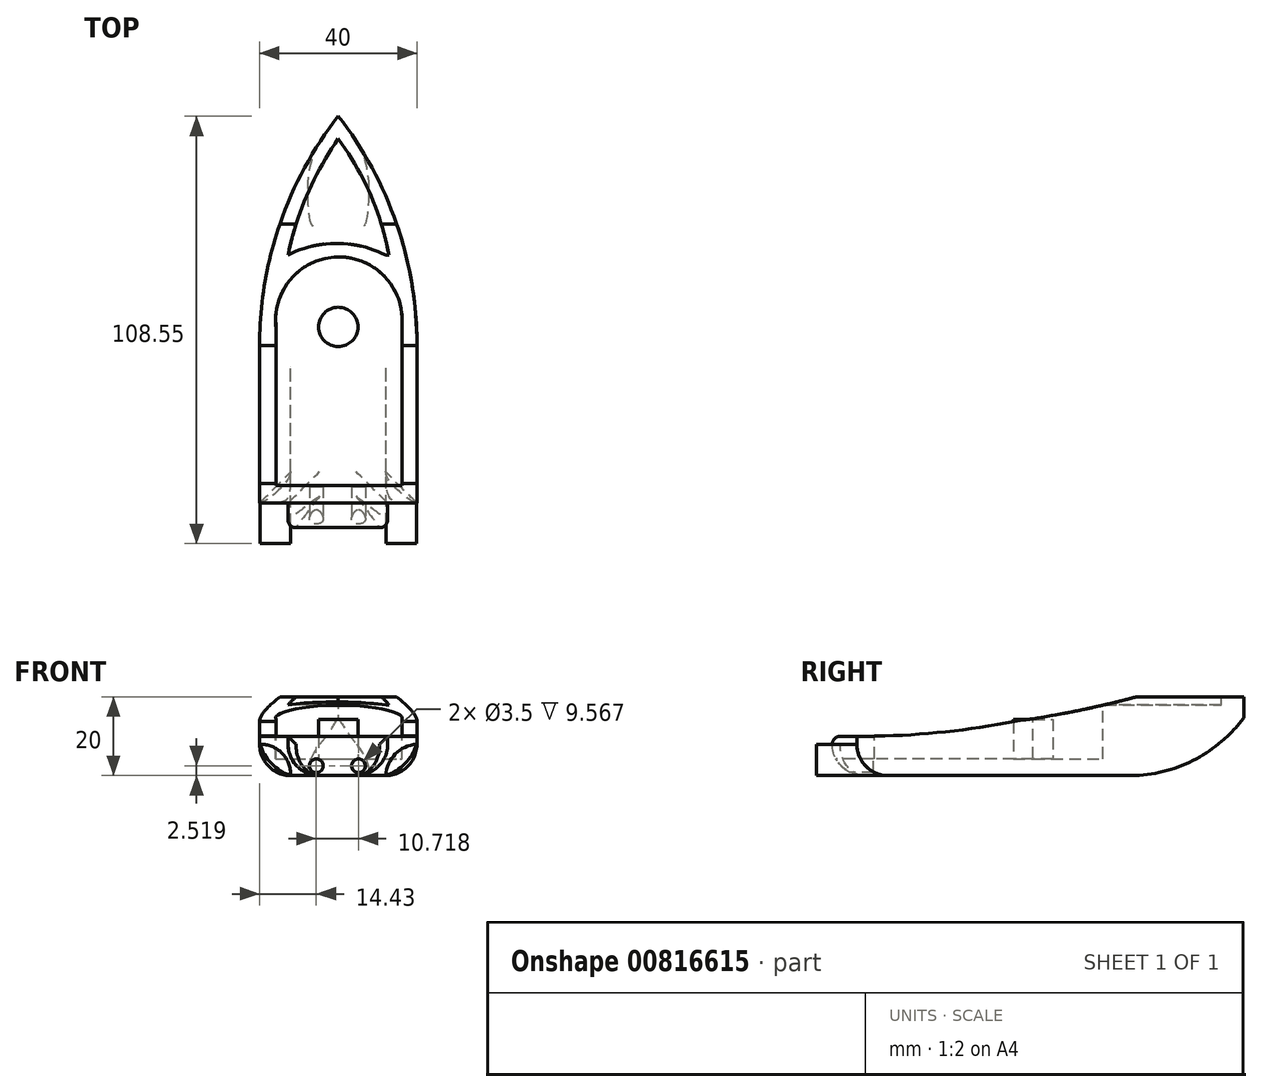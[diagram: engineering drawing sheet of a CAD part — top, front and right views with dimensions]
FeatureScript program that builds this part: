
annotation { "Feature Type Name" : "Feature", "Feature Type Description" : "" }
export const myFeature = defineFeature(function(context is Context, id is Id, definition is map)
    precondition{}
    {
        {
            var Q0;
            Q0=qCreatedBy(makeId("Top.planeOp"),FACE);
            var sketch = newSketch(context, id + "F0", { "sketchPlane" : qUnion([Q0])});
            skLineSegment(sketch, "E0.bottom", {"start": v(-20, 5.24) * mm, "end": v(20, 5.24) * mm});
            skLineSegment(sketch, "E0.top", {"start": v(-20, -34.76) * mm, "end": v(20, -34.76) * mm});
            skLineSegment(sketch, "E0.left", {"start": v(-20, 5.24) * mm, "end": v(-20, -34.76) * mm});
            skLineSegment(sketch, "E0.right", {"start": v(20, 5.24) * mm, "end": v(20, -34.76) * mm});
            skArc(sketch, "E1", {"start": v(0, 63.55) * mm, "mid": v(-14.86, 36.06) * mm, "end": v(-20, 5.24) * mm});
            skArc(sketch, "E2", {"start": v(20, 5.24) * mm, "mid": v(14.86, 36.06) * mm, "end": v(0, 63.55) * mm});
            skLineSegment(sketch, "E3.bottom", {"start": v(-12.77, -34.76) * mm, "end": v(12.55, -34.76) * mm});
            skLineSegment(sketch, "E3.top", {"start": v(-12.77, -40.99) * mm, "end": v(12.55, -40.99) * mm});
            skLineSegment(sketch, "E3.left", {"start": v(-12.77, -34.76) * mm, "end": v(-12.77, -40.99) * mm});
            skLineSegment(sketch, "E3.right", {"start": v(12.55, -34.76) * mm, "end": v(12.55, -40.99) * mm});
            skSolve(sketch);
        }
        {
            var Q0;
            Q0=makeQuery(id+"F0.imprint","IMPRINT",FACE,{"disambiguationData":[TD([[makeQuery(id+"F0.imprint","IMPRINT",EDGE,{"derivedFrom":sQuery(id+"F0.wireOp",EDGE,"E0.bottom")}),1.0]])]});
            var Q1;
            Q1=makeQuery(id+"F0.imprint","IMPRINT",FACE,{"disambiguationData":[TD([[makeQuery(id+"F0.imprint","IMPRINT",EDGE,{"derivedFrom":sQuery(id+"F0.wireOp",EDGE,"E0.bottom")}),-1.0]])]});
            var Q2;
            Q2=makeQuery(id+"F0.imprint","IMPRINT",FACE,{"disambiguationData":[TD([[makeQuery(id+"F0.imprint","IMPRINT",EDGE,{"derivedFrom":sQuery(id+"F0.wireOp",EDGE,"E3.top")}),1.0]])]});
            extrude(context, id + "F1", {"entities" : qUnion([Q0, Q1, Q2]), "depth" : 20 * mm, "offsetDistance" : 25 * mm});
        }
        {
            var Q0;
            Q0=makeQuery(id+"F1.opExtrude","SWEPT_FACE",FACE,{"disambiguationData":[OSD([sQuery(id+"F0.wireOp",EDGE,"E0.left")])]});
            var sketch = newSketch(context, id + "F2", { "sketchPlane" : qUnion([Q0])});
            skArc(sketch, "E4", {"start": v(-5.24, 20) * mm, "mid": v(14.08, 12.3) * mm, "end": v(34.76, 10) * mm});
            skSolve(sketch);
        }
        {
            var Q0;
            {var subQ0=sQuery(id+"F2.wireOp",EDGE,"E4");Q0=makeQuery(id+"F2.imprint","IMPRINT",FACE,{"disambiguationData":[TD([[makeQuery(id+"F2.imprint","IMPRINT",EDGE,{"derivedFrom":subQ0}),1.0]])]});}
            extrude(context, id + "F3", {"entities" : qUnion([Q0]), "operationType" : NewBodyOperationType.REMOVE, "oppositeDirection" : true, "depth" : 40 * mm, "offsetDistance" : 25 * mm});
        }
        {
            var Q0;
            Q0=makeQuery(id+"F1.opExtrude","SWEPT_FACE",FACE,{"disambiguationData":[OSD([sQuery(id+"F0.wireOp",EDGE,"E3.top")])]});
            var sketch = newSketch(context, id + "F4", { "sketchPlane" : qUnion([Q0])});
            skLineSegment(sketch, "E5", {"start": v(-12.77, 10) * mm, "end": v(12.55, 10) * mm});
            skSolve(sketch);
        }
        {
            var Q0;
            {var subQ0=sQuery(id+"F4.wireOp",EDGE,"E5");Q0=makeQuery(id+"F4.imprint","IMPRINT",FACE,{"disambiguationData":[TD([[makeQuery(id+"F4.imprint","IMPRINT",EDGE,{"derivedFrom":subQ0}),1.0]])]});}
            extrude(context, id + "F5", {"entities" : qUnion([Q0]), "operationType" : NewBodyOperationType.REMOVE, "oppositeDirection" : true, "depth" : 7 * mm, "offsetDistance" : 25 * mm});
        }
        {
            var Q0;
            Q0=qCreatedBy(makeId("Right.planeOp"),FACE);
            var sketch = newSketch(context, id + "F6", { "sketchPlane" : qUnion([Q0])});
            skArc(sketch, "E6", {"start": v(-13.16, 12.02) * mm, "mid": v(11.77, 14.75) * mm, "end": v(36.28, 20.03) * mm});
            skArc(sketch, "E7", {"start": v(36.28, 20.03) * mm, "mid": v(10.26, 24.05) * mm, "end": v(-13.16, 12.02) * mm});
            skSolve(sketch);
        }
        {
            var Q0;
            Q0=makeQuery(id+"F6.imprint","IMPRINT",FACE,{"disambiguationData":[TD([[makeQuery(id+"F6.imprint","IMPRINT",EDGE,{"derivedFrom":sQuery(id+"F6.wireOp",EDGE,"E6")}),1.0]])]});
            extrude(context, id + "F7", {"entities" : qUnion([Q0]), "operationType" : NewBodyOperationType.REMOVE, "oppositeDirection" : true, "depth" : 25 * mm, "offsetDistance" : 25 * mm, "hasSecondDirection" : true, "secondDirectionOppositeDirection" : false, "secondDirectionDepth" : 25 * mm});
        }
        {
            var Q0;
            Q0=makeQuery(id+"F1.opExtrude","SWEPT_FACE",FACE,{"disambiguationData":[OSD([sQuery(id+"F0.wireOp",EDGE,"E0.left")])]});
            var sketch = newSketch(context, id + "F8", { "sketchPlane" : qUnion([Q0])});
            skArc(sketch, "E8", {"start": v(-5.24, 13.78) * mm, "mid": v(14.66, 10.9) * mm, "end": v(34.76, 10) * mm});
            skSolve(sketch);
        }
        {
            var Q0;
            {var subQ1=sQuery(id+"F0.wireOp",EDGE,"E0.left");var subQ2=makeQuery(id+"F1.opExtrude","SWEPT_FACE",FACE,{"disambiguationData":[OSD([subQ1])]});var subQ3=makeQuery(id+"F7.boolean.opBoolean","INTERSECT",EDGE,{"derivedFrom":[subQ2,makeQuery(id+"F7.opExtrude","SWEPT_FACE",FACE,{"disambiguationData":[OSD([sQuery(id+"F6.wireOp",EDGE,"E6")])]})]});Q0=makeQuery(id+"F8.imprint","IMPRINT",FACE,{"disambiguationData":[TD([[makeQuery(id+"F8.imprint","IMPRINT",EDGE,{"derivedFrom":subQ3}),1.0]])]});}
            extrude(context, id + "F9", {"entities" : qUnion([Q0]), "operationType" : NewBodyOperationType.REMOVE, "oppositeDirection" : true, "depth" : 40 * mm, "offsetDistance" : 25 * mm});
        }
        {
            var Q0;
            Q0=qCreatedBy(makeId("Right.planeOp"),FACE);
            var sketch = newSketch(context, id + "F10", { "sketchPlane" : qUnion([Q0])});
            skArc(sketch, "E9", {"start": v(35.83, 0) * mm, "mid": v(52, 4.58) * mm, "end": v(64.41, 15.9) * mm});
            skLineSegment(sketch, "E10", {"start": v(64.41, 15.9) * mm, "end": v(64.41, 0) * mm});
            skLineSegment(sketch, "E11", {"start": v(64.41, 0) * mm, "end": v(35.83, 0) * mm});
            skLineSegment(sketch, "E12", {"start": v(35.83, 0) * mm, "end": v(64.41, 0) * mm});
            skSolve(sketch);
        }
        {
            var Q0;
            Q0 = qSketchRegion(id + "F10", true);
            extrude(context, id + "F11", {"entities" : qUnion([Q0]), "operationType" : NewBodyOperationType.REMOVE, "oppositeDirection" : true, "depth" : 25 * mm, "offsetDistance" : 25 * mm, "hasSecondDirection" : true, "secondDirectionOppositeDirection" : false, "secondDirectionDepth" : 25 * mm});
        }
        {
            var Q0;
            Q0=makeQuery(id+"F1.opExtrude","CAP_FACE",FACE,{"disambiguationData":[OSD([sQuery(id+"F0.wireOp",EDGE,"E0.top"),sQuery(id+"F0.wireOp",EDGE,"E0.left"),sQuery(id+"F0.wireOp",EDGE,"E0.right"),sQuery(id+"F0.wireOp",EDGE,"E1"),sQuery(id+"F0.wireOp",EDGE,"E2"),sQuery(id+"F0.wireOp",EDGE,"E3.top"),sQuery(id+"F0.wireOp",EDGE,"E3.left"),sQuery(id+"F0.wireOp",EDGE,"E3.right")])],"isStart":true});
            fillet(context, id + "F12", {"entities" : qUnion([Q0]), "radius" : 8 * mm, "tangentPropagation" : true, "allowEdgeOverflow" : false});
        }
        {
            var Q0;
            Q0=makeQuery(id+"F1.opExtrude","CAP_FACE",FACE,{"disambiguationData":[OSD([sQuery(id+"F0.wireOp",EDGE,"E0.top"),sQuery(id+"F0.wireOp",EDGE,"E0.left"),sQuery(id+"F0.wireOp",EDGE,"E0.right"),sQuery(id+"F0.wireOp",EDGE,"E1"),sQuery(id+"F0.wireOp",EDGE,"E2"),sQuery(id+"F0.wireOp",EDGE,"E3.top"),sQuery(id+"F0.wireOp",EDGE,"E3.left"),sQuery(id+"F0.wireOp",EDGE,"E3.right")])],"isStart":true});
            cPlane(context, id + "F13", {"entities" : qUnion([Q0]), "cplaneType" : CPlaneType.OFFSET, "offset" : 24.3 * mm, "oppositeDirection" : true, "width" : 150 * mm, "height" : 150 * mm});
        }
        {
            var Q0;
            Q0=qCreatedBy(id+"F13.planeOp",FACE);
            var sketch = newSketch(context, id + "F14", { "sketchPlane" : qUnion([Q0])});
            skLineSegment(sketch, "E13.bottom", {"start": v(-15.84, -11.7) * mm, "end": v(16.16, -11.7) * mm});
            skLineSegment(sketch, "E13.top", {"start": v(-15.84, 30.3) * mm, "end": v(16.16, 30.3) * mm});
            skLineSegment(sketch, "E13.left", {"start": v(-15.84, -11.7) * mm, "end": v(-15.84, 30.3) * mm});
            skLineSegment(sketch, "E13.right", {"start": v(16.16, -11.7) * mm, "end": v(16.16, 30.3) * mm});
            skCircle(sketch, "E14", {"center": v(0.16, -11.7) * mm, "radius": 16.09 * mm});
            skSolve(sketch);
        }
        {
            var Q0;
            Q0 = qSketchRegion(id + "F14", true);
            extrude(context, id + "F15", {"entities" : qUnion([Q0]), "operationType" : NewBodyOperationType.REMOVE, "depth" : 20 * mm, "offsetDistance" : 25 * mm});
        }
        {
            var Q0;
            Q0=qCreatedBy(makeId("Front.planeOp"),FACE);
            var sketch = newSketch(context, id + "F16", { "sketchPlane" : qUnion([Q0])});
            skArc(sketch, "E15", {"start": v(-19.87, 7.98) * mm, "mid": v(-16.96, 3.05) * mm, "end": v(-12.12, 0) * mm});
            skArc(sketch, "E16", {"start": v(-12.12, 0) * mm, "mid": v(-14.26, 5.68) * mm, "end": v(-19.87, 7.98) * mm});
            skArc(sketch, "E17", {"start": v(12.08, 0) * mm, "mid": v(16.96, 3.05) * mm, "end": v(19.93, 7.98) * mm});
            skArc(sketch, "E18", {"start": v(19.93, 7.98) * mm, "mid": v(14.5, 5.48) * mm, "end": v(12.08, 0) * mm});
            skSolve(sketch);
        }
        {
            var Q0;
            Q0 = qSketchRegion(id + "F16", true);
            extrude(context, id + "F17", {"entities" : qUnion([Q0]), "operationType" : NewBodyOperationType.ADD, "depth" : 45 * mm, "offsetDistance" : 25 * mm});
        }
        {
            var Q0;
            Q0=makeQuery(id+"F1.opExtrude","SWEPT_FACE",FACE,{"disambiguationData":[OSD([sQuery(id+"F0.wireOp",EDGE,"E3.top")])]});
            fillet(context, id + "F18", {"entities" : qUnion([Q0]), "radius" : 2 * mm, "tangentPropagation" : true, "allowEdgeOverflow" : false});
        }
        {
            var Q0;
            Q0 = qSketchRegion(id + "F14", true);
            extrude(context, id + "F19", {"entities" : qUnion([Q0]), "operationType" : NewBodyOperationType.REMOVE, "depth" : 20 * mm, "offsetDistance" : 25 * mm});
        }
        {
            var Q0;
            {var subQ0=sQuery(id+"F0.wireOp",EDGE,"E2");var subQ1=sQuery(id+"F0.wireOp",EDGE,"E1");var subQ2=sQuery(id+"F0.wireOp",EDGE,"E0.right");var subQ3=sQuery(id+"F0.wireOp",EDGE,"E0.left");Q0=makeQuery(id+"F3.boolean.opBoolean","SPLIT",FACE,{"disambiguationData":[TD([makeQuery(id+"F1.opExtrude","SWEPT_FACE",FACE,{"disambiguationData":[OSD([subQ3])]})])],"derivedFrom":makeQuery(id+"F1.opExtrude","CAP_FACE",FACE,{"disambiguationData":[OSD([sQuery(id+"F0.wireOp",EDGE,"E0.top"),subQ3,subQ2,subQ1,subQ0,sQuery(id+"F0.wireOp",EDGE,"E3.top"),sQuery(id+"F0.wireOp",EDGE,"E3.left"),sQuery(id+"F0.wireOp",EDGE,"E3.right")])],"isStart":false})});}
            var sketch = newSketch(context, id + "F20", { "sketchPlane" : qUnion([Q0])});
            skArc(sketch, "E19", {"start": v(0, 57.83) * mm, "mid": v(-7.88, 43.7) * mm, "end": v(-12.76, 28.3) * mm});
            skArc(sketch, "E20", {"start": v(12.97, 27.75) * mm, "mid": v(8.21, 43.53) * mm, "end": v(0, 57.83) * mm});
            skArc(sketch, "E21", {"start": v(12.97, 27.75) * mm, "mid": v(0.17, 31.22) * mm, "end": v(-12.76, 28.3) * mm});
            skSolve(sketch);
        }
        {
            var Q0;
            Q0 = qSketchRegion(id + "F20", true);
            extrude(context, id + "F21", {"entities" : qUnion([Q0]), "operationType" : NewBodyOperationType.REMOVE, "oppositeDirection" : true, "depth" : 2 * mm, "offsetDistance" : 25 * mm});
        }
        {
            var Q0;
            {var subQ0=sQuery(id+"F14.wireOp",EDGE,"E14");var subQ1=sQuery(id+"F14.wireOp",EDGE,"E13.right");var subQ2=sQuery(id+"F14.wireOp",EDGE,"E13.left");var subQ3=sQuery(id+"F14.wireOp",EDGE,"E13.top");Q0=makeQuery(id+"F19.boolean.opBoolean","MERGE",FACE,{"derivedFrom":[makeQuery(id+"F15.boolean.opBoolean","COPY",FACE,{"derivedFrom":makeQuery(id+"F15.opExtrude","CAP_FACE",FACE,{"disambiguationData":[OSD([subQ3,subQ2,subQ1,subQ0])],"isStart":false})}),makeQuery(id+"F19.opExtrude","CAP_FACE",FACE,{"disambiguationData":[OSD([subQ3,subQ2,subQ1,subQ0])],"isStart":false})]});}
            var sketch = newSketch(context, id + "F22", { "sketchPlane" : qUnion([Q0])});
            skCircle(sketch, "E22", {"center": v(0, 10) * mm, "radius": 5 * mm});
            skSolve(sketch);
        }
        {
            var Q0;
            Q0 = qSketchRegion(id + "F22", true);
            extrude(context, id + "F23", {"entities" : qUnion([Q0]), "operationType" : NewBodyOperationType.ADD, "depth" : 10 * mm, "offsetDistance" : 25 * mm});
        }
        {
            var Q0;
            Q0=makeQuery(id+"F17.opExtrude","CAP_FACE",FACE,{"disambiguationData":[OSD([sQuery(id+"F16.wireOp",EDGE,"E15"),sQuery(id+"F16.wireOp",EDGE,"E16")])],"isStart":false});
            cPlane(context, id + "F24", {"entities" : qUnion([Q0]), "cplaneType" : CPlaneType.OFFSET, "offset" : 4.5 * mm, "oppositeDirection" : true, "width" : 150 * mm, "height" : 150 * mm});
        }
        {
            var Q0;
            Q0=qCreatedBy(id+"F24.planeOp",FACE);
            var sketch = newSketch(context, id + "F25", { "sketchPlane" : qUnion([Q0])});
            skCircle(sketch, "E23", {"center": v(-5.57, 2.52) * mm, "radius": 1.75 * mm});
            skCircle(sketch, "E24", {"center": v(5.15, 2.52) * mm, "radius": 1.75 * mm});
            skSolve(sketch);
        }
        {
            var Q0;
            Q0 = qSketchRegion(id + "F25", true);
            extrude(context, id + "F26", {"entities" : qUnion([Q0]), "operationType" : NewBodyOperationType.REMOVE, "oppositeDirection" : true, "depth" : 10 * mm, "offsetDistance" : 25 * mm});
        }
    });
